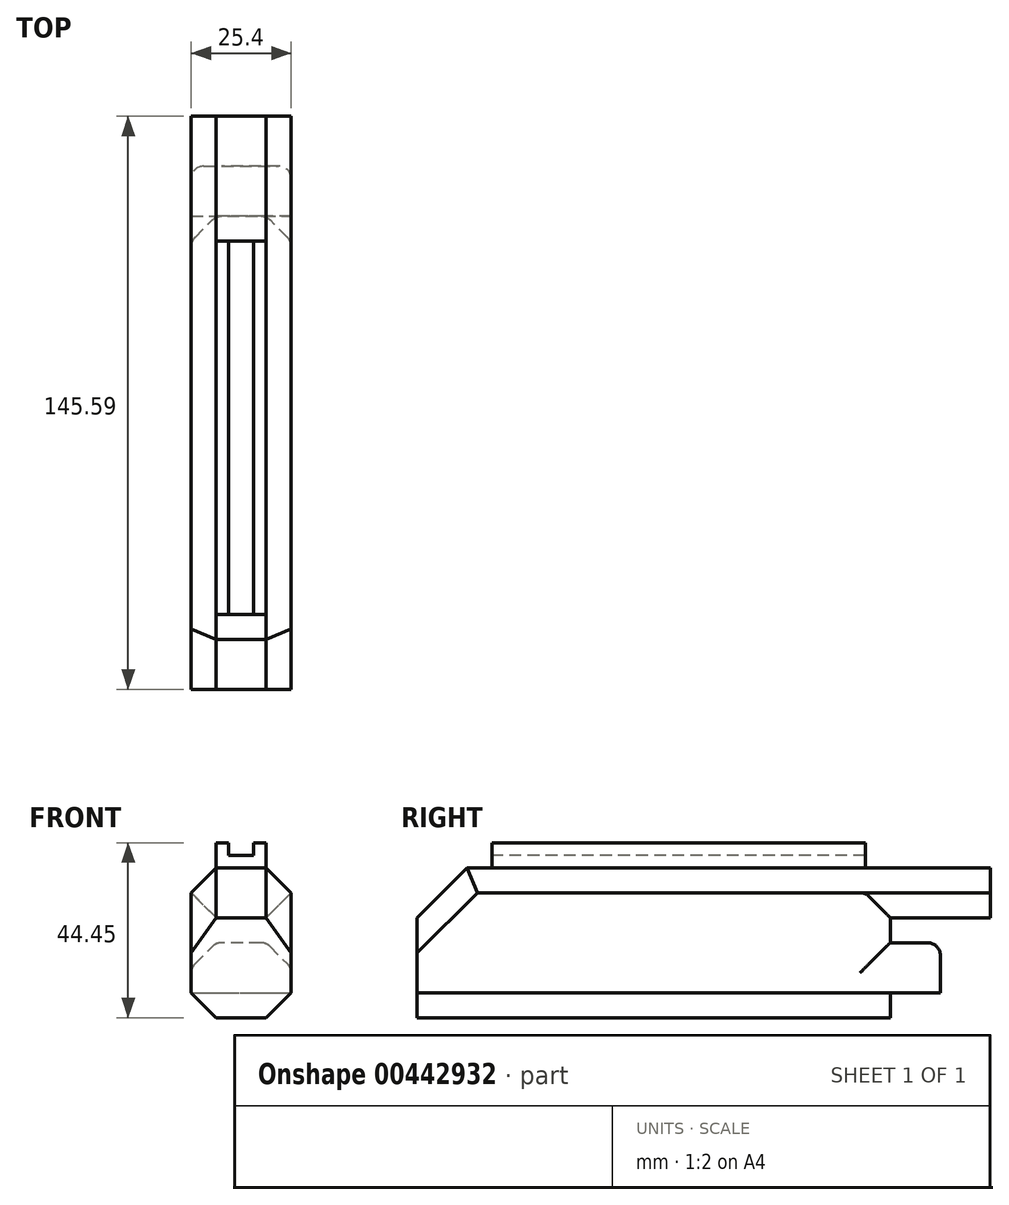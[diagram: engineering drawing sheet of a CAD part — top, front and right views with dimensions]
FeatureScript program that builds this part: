
annotation { "Feature Type Name" : "Feature", "Feature Type Description" : "" }
export const myFeature = defineFeature(function(context is Context, id is Id, definition is map)
    precondition{}
    {
        {
            var Q0;
            Q0=qCreatedBy(makeId("Right.planeOp"),FACE);
            var sketch = newSketch(context, id + "F0", { "sketchPlane" : qUnion([Q0])});
            skLineSegment(sketch, "E0", {"start": v(0, 0) * mm, "end": v(76.2, 0) * mm});
            skLineSegment(sketch, "E1", {"start": v(0, 0) * mm, "end": v(0, 25.4) * mm});
            skLineSegment(sketch, "E2", {"start": v(0, 25.4) * mm, "end": v(12.7, 38.1) * mm});
            skLineSegment(sketch, "E3", {"start": v(12.7, 38.1) * mm, "end": v(120.2, 38.1) * mm});
            skLineSegment(sketch, "E4", {"start": v(19.05, 38.1) * mm, "end": v(19.05, 44.45) * mm});
            skLineSegment(sketch, "E5", {"start": v(19.05, 44.45) * mm, "end": v(113.84, 44.45) * mm});
            skLineSegment(sketch, "E6", {"start": v(113.84, 44.45) * mm, "end": v(113.84, 38.1) * mm});
            skLineSegment(sketch, "E7", {"start": v(76.2, 0) * mm, "end": v(120.2, 0) * mm});
            skLineSegment(sketch, "E8", {"start": v(120.2, 0) * mm, "end": v(120.2, 38.1) * mm});
            skSolve(sketch);
        }
        {
            var Q0;
            Q0=makeQuery(id+"F0.imprint","IMPRINT",FACE,{"disambiguationData":[TD([[makeQuery(id+"F0.imprint","IMPRINT",EDGE,{"derivedFrom":sQuery(id+"F0.wireOp",EDGE,"E0")}),1.0]])]});
            extrude(context, id + "F1", {"entities" : qUnion([Q0]), "endBound" : BoundingType.SYMMETRIC, "depth" : 25.4 * mm});
        }
        {
            var Q0;
            {var subQ0=sQuery(id+"F0.wireOp",EDGE,"E4");Q0=makeQuery(id+"F0.imprint","IMPRINT",FACE,{"disambiguationData":[TD([[makeQuery(id+"F0.imprint","IMPRINT",EDGE,{"derivedFrom":subQ0}),-1.0]])]});}
            extrude(context, id + "F2", {"entities" : qUnion([Q0]), "operationType" : NewBodyOperationType.ADD, "endBound" : BoundingType.SYMMETRIC, "depth" : 12.7 * mm});
        }
        {
            var Q0;
            Q0=makeQuery(id+"F2.opExtrude","SWEPT_FACE",FACE,{"disambiguationData":[OSD([sQuery(id+"F0.wireOp",EDGE,"E4")])]});
            var sketch = newSketch(context, id + "F3", { "sketchPlane" : qUnion([Q0])});
            skLineSegment(sketch, "E9.0", {"start": v(6.35, 44.45) * mm, "end": v(-6.35, 44.45) * mm});
            skLineSegment(sketch, "E10.0", {"start": v(6.35, 38.1) * mm, "end": v(6.35, 44.45) * mm});
            skLineSegment(sketch, "E11.0", {"start": v(-6.35, 38.1) * mm, "end": v(-6.35, 44.45) * mm});
            skLineSegment(sketch, "E12", {"start": v(-3.18, 44.45) * mm, "end": v(-3.17, 41.28) * mm});
            skLineSegment(sketch, "E13", {"start": v(-3.17, 41.28) * mm, "end": v(3.18, 41.28) * mm});
            skLineSegment(sketch, "E14", {"start": v(3.18, 41.28) * mm, "end": v(3.18, 44.45) * mm});
            skLineSegment(sketch, "E15", {"start": v(-3.18, 44.45) * mm, "end": v(3.18, 44.45) * mm});
            skSolve(sketch);
        }
        {
            var Q0;
            Q0=makeQuery(id+"F3.imprint","IMPRINT",FACE,{"disambiguationData":[TD([[makeQuery(id+"F3.imprint","IMPRINT",EDGE,{"derivedFrom":sQuery(id+"F3.wireOp",EDGE,"E12")}),1.0]])]});
            extrude(context, id + "F4", {"entities" : qUnion([Q0]), "operationType" : NewBodyOperationType.REMOVE, "endBound" : BoundingType.UP_TO_NEXT, "oppositeDirection" : true, "depth" : 25.4 * mm});
        }
        {
            var Q0;
            Q0=makeQuery(id+"F1.opExtrude","CAP_EDGE",EDGE,{"disambiguationData":[OSD([sQuery(id+"F0.wireOp",EDGE,"E2")])],"isStart":true});
            var Q1;
            Q1=makeQuery(id+"F1.opExtrude","CAP_EDGE",EDGE,{"disambiguationData":[OSD([sQuery(id+"F0.wireOp",EDGE,"E2")])],"isStart":false});
            var Q2;
            Q2=makeQuery(id+"F1.opExtrude","CAP_EDGE",EDGE,{"disambiguationData":[OSD([sQuery(id+"F0.wireOp",EDGE,"E3")])],"isStart":true});
            var Q3;
            Q3=makeQuery(id+"F1.opExtrude","CAP_EDGE",EDGE,{"disambiguationData":[OSD([sQuery(id+"F0.wireOp",EDGE,"E3")])],"isStart":false});
            var Q4;
            Q4=makeQuery(id+"F1.opExtrude","CAP_EDGE",EDGE,{"disambiguationData":[OSD([sQuery(id+"F0.wireOp",EDGE,"E0")])],"isStart":true});
            var Q5;
            Q5=makeQuery(id+"F1.opExtrude","CAP_EDGE",EDGE,{"disambiguationData":[OSD([sQuery(id+"F0.wireOp",EDGE,"E0")])],"isStart":false});
            var Q6;
            Q6=makeQuery(id+"F1.opExtrude","CAP_EDGE",EDGE,{"disambiguationData":[OSD([sQuery(id+"F0.wireOp",EDGE,"qCiKrhhC-vUk0-I7n4-36jf-ZsMYgUOT2Ggz")])],"isStart":false});
            var Q7;
            Q7=makeQuery(id+"F1.opExtrude","CAP_EDGE",EDGE,{"disambiguationData":[OSD([sQuery(id+"F0.wireOp",EDGE,"qCiKrhhC-vUk0-I7n4-36jf-ZsMYgUOT2Ggz")])],"isStart":true});
            chamfer(context, id + "F5", {"entities" : qUnion([Q0, Q1, Q2, Q3, Q4, Q5, Q6, Q7]), "width" : 6.35 * mm, "tangentPropagation" : true});
        }
        {
            var Q0;
            Q0=makeQuery(id+"F1.opExtrude","SWEPT_FACE",FACE,{"disambiguationData":[OSD([sQuery(id+"F0.wireOp",EDGE,"E8")])]});
            var sketch = newSketch(context, id + "F6", { "sketchPlane" : qUnion([Q0])});
            skLineSegment(sketch, "E16.0", {"start": v(-6.35, 38.1) * mm, "end": v(6.35, 38.1) * mm});
            skLineSegment(sketch, "E17.0", {"start": v(12.7, 31.75) * mm, "end": v(6.35, 38.1) * mm});
            skLineSegment(sketch, "E18.0", {"start": v(-6.35, 38.1) * mm, "end": v(-12.7, 31.75) * mm});
            skLineSegment(sketch, "E19", {"start": v(-12.7, 31.75) * mm, "end": v(-6.35, 25.4) * mm});
            skLineSegment(sketch, "E20", {"start": v(-6.35, 25.4) * mm, "end": v(6.35, 25.4) * mm});
            skLineSegment(sketch, "E21", {"start": v(6.35, 25.4) * mm, "end": v(12.7, 31.75) * mm});
            skSolve(sketch);
        }
        {
            var Q0;
            Q0=makeQuery(id+"F6.imprint","IMPRINT",FACE,{"disambiguationData":[TD([[makeQuery(id+"F6.imprint","IMPRINT",EDGE,{"derivedFrom":sQuery(id+"F6.wireOp",EDGE,"E16.0")}),-1.0]])]});
            extrude(context, id + "F7", {"entities" : qUnion([Q0]), "operationType" : NewBodyOperationType.ADD, "depth" : 25.4 * mm});
        }
        {
            var Q0;
            Q0=makeQuery(id+"F1.opExtrude","SWEPT_FACE",FACE,{"disambiguationData":[OSD([sQuery(id+"F0.wireOp",EDGE,"E8")])]});
            var sketch = newSketch(context, id + "F8", { "sketchPlane" : qUnion([Q0])});
            skLineSegment(sketch, "E22", {"start": v(12.7, 6.35) * mm, "end": v(-12.7, 6.35) * mm});
            skLineSegment(sketch, "E23", {"start": v(-12.7, 6.35) * mm, "end": v(-12.7, 19.05) * mm});
            skLineSegment(sketch, "E24", {"start": v(-12.7, 19.05) * mm, "end": v(12.7, 19.05) * mm});
            skLineSegment(sketch, "E25", {"start": v(12.7, 19.05) * mm, "end": v(12.7, 6.35) * mm});
            skSolve(sketch);
        }
        {
            var Q0;
            Q0=makeQuery(id+"F8.imprint","IMPRINT",FACE,{"disambiguationData":[TD([[makeQuery(id+"F8.imprint","IMPRINT",EDGE,{"derivedFrom":sQuery(id+"F8.wireOp",EDGE,"E22")}),-1.0]])]});
            extrude(context, id + "F9", {"entities" : qUnion([Q0]), "operationType" : NewBodyOperationType.ADD, "depth" : 12.7 * mm});
        }
        {
            var Q0;
            Q0=makeQuery(id+"F9.opExtrude","SWEPT_EDGE",EDGE,{"disambiguationData":[OSD([sQuery(id+"F0.wireOp",EDGE,"E8"),sQuery(id+"F8.wireOp",EDGE,"E24"),sQuery(id+"F8.wireOp",EDGE,"E25")])]});
            var Q1;
            Q1=makeQuery(id+"F9.opExtrude","SWEPT_EDGE",EDGE,{"disambiguationData":[OSD([sQuery(id+"F0.wireOp",EDGE,"E8"),sQuery(id+"F8.wireOp",EDGE,"E23"),sQuery(id+"F8.wireOp",EDGE,"E24")])]});
            var Q2;
            Q2=makeQuery(id+"F1.opExtrude","CAP_EDGE",EDGE,{"disambiguationData":[OSD([sQuery(id+"F0.wireOp",EDGE,"E8")])],"isStart":false});
            var Q3;
            Q3=makeQuery(id+"F1.opExtrude","CAP_EDGE",EDGE,{"disambiguationData":[OSD([sQuery(id+"F0.wireOp",EDGE,"E8")])],"isStart":true});
            chamfer(context, id + "F10", {"entities" : qUnion([Q0, Q1, Q2, Q3]), "width" : 6.35 * mm, "tangentPropagation" : true});
        }
        {
            var Q0;
            {var subQ0=sQuery(id+"F0.wireOp",EDGE,"E8");Q0=makeQuery(id+"F10.opChamfer","BLEND_EDGE",EDGE,{"blendedFrom":[makeQuery(id+"F1.opExtrude","CAP_EDGE",EDGE,{"disambiguationData":[OSD([subQ0])],"isStart":true}),makeQuery(id+"F9.boolean.opBoolean","MERGE",FACE,{"derivedFrom":[makeQuery(id+"F1.opExtrude","CAP_FACE",FACE,{"disambiguationData":[OSD([sQuery(id+"F0.wireOp",EDGE,"E0"),sQuery(id+"F0.wireOp",EDGE,"E1"),sQuery(id+"F0.wireOp",EDGE,"E2"),sQuery(id+"F0.wireOp",EDGE,"E3"),sQuery(id+"F0.wireOp",EDGE,"E7"),subQ0])],"isStart":true}),makeQuery(id+"F9.opExtrude","SWEPT_FACE",FACE,{"disambiguationData":[OSD([sQuery(id+"F8.wireOp",EDGE,"E25")])]})]})],"blendedInto":[makeQuery(id+"F9.boolean.opBoolean","MERGE",FACE,{"derivedFrom":[makeQuery(id+"F1.opExtrude","CAP_FACE",FACE,{"disambiguationData":[OSD([sQuery(id+"F0.wireOp",EDGE,"E0"),sQuery(id+"F0.wireOp",EDGE,"E1"),sQuery(id+"F0.wireOp",EDGE,"E2"),sQuery(id+"F0.wireOp",EDGE,"E3"),sQuery(id+"F0.wireOp",EDGE,"E7"),subQ0])],"isStart":true}),makeQuery(id+"F9.opExtrude","SWEPT_FACE",FACE,{"disambiguationData":[OSD([sQuery(id+"F8.wireOp",EDGE,"E25")])]})]})]});}
            var Q1;
            {var subQ0=sQuery(id+"F8.wireOp",EDGE,"E25");var subQ1=sQuery(id+"F0.wireOp",EDGE,"E8");Q1=makeQuery(id+"F10.opChamfer","BLEND_EDGE",EDGE,{"blendedFrom":[makeQuery(id+"F9.opExtrude","SWEPT_EDGE",EDGE,{"disambiguationData":[OSD([subQ1,sQuery(id+"F8.wireOp",EDGE,"E24"),subQ0])]}),makeQuery(id+"F9.boolean.opBoolean","MERGE",FACE,{"derivedFrom":[makeQuery(id+"F1.opExtrude","CAP_FACE",FACE,{"disambiguationData":[OSD([sQuery(id+"F0.wireOp",EDGE,"E0"),sQuery(id+"F0.wireOp",EDGE,"E1"),sQuery(id+"F0.wireOp",EDGE,"E2"),sQuery(id+"F0.wireOp",EDGE,"E3"),sQuery(id+"F0.wireOp",EDGE,"E7"),subQ1])],"isStart":true}),makeQuery(id+"F9.opExtrude","SWEPT_FACE",FACE,{"disambiguationData":[OSD([subQ0])]})]})],"blendedInto":[makeQuery(id+"F9.boolean.opBoolean","MERGE",FACE,{"derivedFrom":[makeQuery(id+"F1.opExtrude","CAP_FACE",FACE,{"disambiguationData":[OSD([sQuery(id+"F0.wireOp",EDGE,"E0"),sQuery(id+"F0.wireOp",EDGE,"E1"),sQuery(id+"F0.wireOp",EDGE,"E2"),sQuery(id+"F0.wireOp",EDGE,"E3"),sQuery(id+"F0.wireOp",EDGE,"E7"),subQ1])],"isStart":true}),makeQuery(id+"F9.opExtrude","SWEPT_FACE",FACE,{"disambiguationData":[OSD([subQ0])]})]})]});}
            var Q2;
            {var subQ0=sQuery(id+"F8.wireOp",EDGE,"E24");Q2=makeQuery(id+"F10.opChamfer","BLEND_EDGE",EDGE,{"blendedFrom":[makeQuery(id+"F9.opExtrude","SWEPT_EDGE",EDGE,{"disambiguationData":[OSD([sQuery(id+"F0.wireOp",EDGE,"E8"),subQ0,sQuery(id+"F8.wireOp",EDGE,"E25")])]}),makeQuery(id+"F9.opExtrude","SWEPT_FACE",FACE,{"disambiguationData":[OSD([subQ0])]})],"blendedInto":[makeQuery(id+"F9.opExtrude","SWEPT_FACE",FACE,{"disambiguationData":[OSD([subQ0])]})]});}
            var Q3;
            {var subQ0=sQuery(id+"F0.wireOp",EDGE,"E8");Q3=makeQuery(id+"F10.opChamfer","BLEND_EDGE",EDGE,{"blendedFrom":[makeQuery(id+"F1.opExtrude","CAP_EDGE",EDGE,{"disambiguationData":[OSD([subQ0])],"isStart":true}),makeQuery(id+"F9.boolean.opBoolean","SPLIT",FACE,{"disambiguationData":[TD([makeQuery(id+"F7.opExtrude","SWEPT_FACE",FACE,{"disambiguationData":[OSD([sQuery(id+"F6.wireOp",EDGE,"E17.0")])]})])],"derivedFrom":makeQuery(id+"F1.opExtrude","SWEPT_FACE",FACE,{"disambiguationData":[OSD([subQ0])]})})],"blendedInto":[makeQuery(id+"F9.boolean.opBoolean","SPLIT",FACE,{"disambiguationData":[TD([makeQuery(id+"F7.opExtrude","SWEPT_FACE",FACE,{"disambiguationData":[OSD([sQuery(id+"F6.wireOp",EDGE,"E17.0")])]})])],"derivedFrom":makeQuery(id+"F1.opExtrude","SWEPT_FACE",FACE,{"disambiguationData":[OSD([subQ0])]})})]});}
            var Q4;
            Q4=makeQuery(id+"F7.opExtrude","SWEPT_EDGE",EDGE,{"disambiguationData":[OSD([sQuery(id+"F6.wireOp",EDGE,"E20"),sQuery(id+"F6.wireOp",EDGE,"E21")])]});
            var Q5;
            {var subQ0=sQuery(id+"F0.wireOp",EDGE,"E8");Q5=makeQuery(id+"F10.opChamfer","BLEND_EDGE",EDGE,{"blendedFrom":[makeQuery(id+"F1.opExtrude","CAP_EDGE",EDGE,{"disambiguationData":[OSD([subQ0])],"isStart":false}),makeQuery(id+"F9.boolean.opBoolean","SPLIT",FACE,{"disambiguationData":[TD([makeQuery(id+"F7.opExtrude","SWEPT_FACE",FACE,{"disambiguationData":[OSD([sQuery(id+"F6.wireOp",EDGE,"E17.0")])]})])],"derivedFrom":makeQuery(id+"F1.opExtrude","SWEPT_FACE",FACE,{"disambiguationData":[OSD([subQ0])]})})],"blendedInto":[makeQuery(id+"F9.boolean.opBoolean","SPLIT",FACE,{"disambiguationData":[TD([makeQuery(id+"F7.opExtrude","SWEPT_FACE",FACE,{"disambiguationData":[OSD([sQuery(id+"F6.wireOp",EDGE,"E17.0")])]})])],"derivedFrom":makeQuery(id+"F1.opExtrude","SWEPT_FACE",FACE,{"disambiguationData":[OSD([subQ0])]})})]});}
            var Q6;
            Q6=makeQuery(id+"F7.opExtrude","SWEPT_EDGE",EDGE,{"disambiguationData":[OSD([sQuery(id+"F6.wireOp",EDGE,"E19"),sQuery(id+"F6.wireOp",EDGE,"E20")])]});
            var Q7;
            {var subQ0=sQuery(id+"F8.wireOp",EDGE,"E24");Q7=makeQuery(id+"F10.opChamfer","BLEND_EDGE",EDGE,{"blendedFrom":[makeQuery(id+"F9.opExtrude","SWEPT_EDGE",EDGE,{"disambiguationData":[OSD([sQuery(id+"F0.wireOp",EDGE,"E8"),sQuery(id+"F8.wireOp",EDGE,"E23"),subQ0])]}),makeQuery(id+"F9.opExtrude","SWEPT_FACE",FACE,{"disambiguationData":[OSD([subQ0])]})],"blendedInto":[makeQuery(id+"F9.opExtrude","SWEPT_FACE",FACE,{"disambiguationData":[OSD([subQ0])]})]});}
            var Q8;
            {var subQ0=sQuery(id+"F0.wireOp",EDGE,"E8");Q8=makeQuery(id+"F10.opChamfer","BLEND_EDGE",EDGE,{"blendedFrom":[makeQuery(id+"F1.opExtrude","CAP_EDGE",EDGE,{"disambiguationData":[OSD([subQ0])],"isStart":false}),makeQuery(id+"F9.boolean.opBoolean","MERGE",FACE,{"derivedFrom":[makeQuery(id+"F1.opExtrude","CAP_FACE",FACE,{"disambiguationData":[OSD([sQuery(id+"F0.wireOp",EDGE,"E0"),sQuery(id+"F0.wireOp",EDGE,"E1"),sQuery(id+"F0.wireOp",EDGE,"E2"),sQuery(id+"F0.wireOp",EDGE,"E3"),sQuery(id+"F0.wireOp",EDGE,"E7"),subQ0])],"isStart":false}),makeQuery(id+"F9.opExtrude","SWEPT_FACE",FACE,{"disambiguationData":[OSD([sQuery(id+"F8.wireOp",EDGE,"E23")])]})]})],"blendedInto":[makeQuery(id+"F9.boolean.opBoolean","MERGE",FACE,{"derivedFrom":[makeQuery(id+"F1.opExtrude","CAP_FACE",FACE,{"disambiguationData":[OSD([sQuery(id+"F0.wireOp",EDGE,"E0"),sQuery(id+"F0.wireOp",EDGE,"E1"),sQuery(id+"F0.wireOp",EDGE,"E2"),sQuery(id+"F0.wireOp",EDGE,"E3"),sQuery(id+"F0.wireOp",EDGE,"E7"),subQ0])],"isStart":false}),makeQuery(id+"F9.opExtrude","SWEPT_FACE",FACE,{"disambiguationData":[OSD([sQuery(id+"F8.wireOp",EDGE,"E23")])]})]})]});}
            var Q9;
            {var subQ0=sQuery(id+"F8.wireOp",EDGE,"E23");var subQ1=sQuery(id+"F0.wireOp",EDGE,"E8");Q9=makeQuery(id+"F10.opChamfer","BLEND_EDGE",EDGE,{"blendedFrom":[makeQuery(id+"F9.opExtrude","SWEPT_EDGE",EDGE,{"disambiguationData":[OSD([subQ1,subQ0,sQuery(id+"F8.wireOp",EDGE,"E24")])]}),makeQuery(id+"F9.boolean.opBoolean","MERGE",FACE,{"derivedFrom":[makeQuery(id+"F1.opExtrude","CAP_FACE",FACE,{"disambiguationData":[OSD([sQuery(id+"F0.wireOp",EDGE,"E0"),sQuery(id+"F0.wireOp",EDGE,"E1"),sQuery(id+"F0.wireOp",EDGE,"E2"),sQuery(id+"F0.wireOp",EDGE,"E3"),sQuery(id+"F0.wireOp",EDGE,"E7"),subQ1])],"isStart":false}),makeQuery(id+"F9.opExtrude","SWEPT_FACE",FACE,{"disambiguationData":[OSD([subQ0])]})]})],"blendedInto":[makeQuery(id+"F9.boolean.opBoolean","MERGE",FACE,{"derivedFrom":[makeQuery(id+"F1.opExtrude","CAP_FACE",FACE,{"disambiguationData":[OSD([sQuery(id+"F0.wireOp",EDGE,"E0"),sQuery(id+"F0.wireOp",EDGE,"E1"),sQuery(id+"F0.wireOp",EDGE,"E2"),sQuery(id+"F0.wireOp",EDGE,"E3"),sQuery(id+"F0.wireOp",EDGE,"E7"),subQ1])],"isStart":false}),makeQuery(id+"F9.opExtrude","SWEPT_FACE",FACE,{"disambiguationData":[OSD([subQ0])]})]})]});}
            var Q10;
            Q10=makeQuery(id+"F9.opExtrude","CAP_EDGE",EDGE,{"disambiguationData":[OSD([sQuery(id+"F8.wireOp",EDGE,"E24")])],"isStart":false});
            var Q11;
            {var subQ0=sQuery(id+"F8.wireOp",EDGE,"E25");var subQ1=sQuery(id+"F8.wireOp",EDGE,"E24");Q11=makeQuery(id+"F10.opChamfer","BLEND_EDGE",EDGE,{"blendedFrom":[makeQuery(id+"F9.opExtrude","SWEPT_EDGE",EDGE,{"disambiguationData":[OSD([sQuery(id+"F0.wireOp",EDGE,"E8"),subQ1,subQ0])]}),makeQuery(id+"F9.opExtrude","CAP_FACE",FACE,{"disambiguationData":[OSD([sQuery(id+"F8.wireOp",EDGE,"E22"),sQuery(id+"F8.wireOp",EDGE,"E23"),subQ1,subQ0])],"isStart":false})],"blendedInto":[makeQuery(id+"F9.opExtrude","CAP_FACE",FACE,{"disambiguationData":[OSD([sQuery(id+"F8.wireOp",EDGE,"E22"),sQuery(id+"F8.wireOp",EDGE,"E23"),subQ1,subQ0])],"isStart":false})]});}
            var Q12;
            {var subQ0=sQuery(id+"F8.wireOp",EDGE,"E24");var subQ1=sQuery(id+"F8.wireOp",EDGE,"E23");Q12=makeQuery(id+"F10.opChamfer","BLEND_EDGE",EDGE,{"blendedFrom":[makeQuery(id+"F9.opExtrude","SWEPT_EDGE",EDGE,{"disambiguationData":[OSD([sQuery(id+"F0.wireOp",EDGE,"E8"),subQ1,subQ0])]}),makeQuery(id+"F9.opExtrude","CAP_FACE",FACE,{"disambiguationData":[OSD([sQuery(id+"F8.wireOp",EDGE,"E22"),subQ1,subQ0,sQuery(id+"F8.wireOp",EDGE,"E25")])],"isStart":false})],"blendedInto":[makeQuery(id+"F9.opExtrude","CAP_FACE",FACE,{"disambiguationData":[OSD([sQuery(id+"F8.wireOp",EDGE,"E22"),subQ1,subQ0,sQuery(id+"F8.wireOp",EDGE,"E25")])],"isStart":false})]});}
            var Q13;
            Q13=makeQuery(id+"F9.opExtrude","CAP_EDGE",EDGE,{"disambiguationData":[OSD([sQuery(id+"F8.wireOp",EDGE,"E23")])],"isStart":false});
            var Q14;
            Q14=makeQuery(id+"F9.opExtrude","CAP_EDGE",EDGE,{"disambiguationData":[OSD([sQuery(id+"F8.wireOp",EDGE,"E25")])],"isStart":false});
            fillet(context, id + "F11", {"entities" : qUnion([Q0, Q1, Q2, Q3, Q4, Q5, Q6, Q7, Q8, Q9, Q10, Q11, Q12, Q13, Q14]), "radius" : 3.17 * mm, "tangentPropagation" : true, "allowEdgeOverflow" : false});
        }
    });
